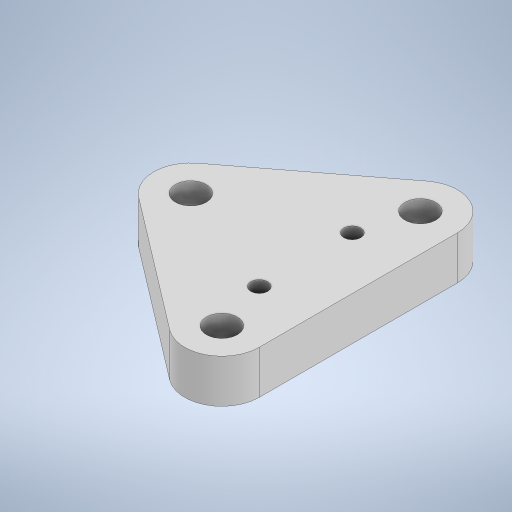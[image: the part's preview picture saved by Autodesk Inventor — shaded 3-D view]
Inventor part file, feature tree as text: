
AUTODESK INVENTOR PART (.ipt)
format: ipt  version: 2023.2 (Build 272271030, 271C)  size: 276,992 bytes
history: native  units: mm
features: extrude x3, sketch x3, projected_geometry x2
ambient origin geometry x8: Origin, YZ Plane, XZ Plane, XY Plane, X Axis, Y Axis, Z Axis, Center Point
bodies: Solid1 (feature_tree)
feature tree (8):
  extrude  "Extrusion1"  Depth=10.0mm
  extrude  "Extrusion2"  Depth=32.0mm
  extrude  "Extrusion3"  Depth=14.0mm TaperAngle=0.0deg
  sketch  "Sketch1"  dims[d0=10.0mm d1=64.0mm]
  sketch  "Sketch3"  dims[d2=32.0mm d3=24.0mm]
  projected_geometry  "Projected Loop1"
  sketch  "Sketch4"  dims[d4=42.0mm d5=14.0mm d6=0.0mm d7=10.0mm d8=40.0mm d9=5.5mm d10=5.0mm d11=6.95mm d12=0.0mm d13=0.0mm d14=8.1mm d15=3.0mm d16=0.0mm]
  projected_geometry  "Projected Loop2"
